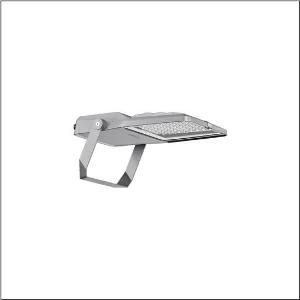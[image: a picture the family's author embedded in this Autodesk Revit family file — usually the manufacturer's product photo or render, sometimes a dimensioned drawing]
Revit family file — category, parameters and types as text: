
# Revit family: floodlight_fl_21_iq_mini___pl64_5xa7771c4e1a_d4bc
name_source: partatom
category: Lighting Fixtures
units: mm (PartAtom-declared; Revit-internal decimal feet)

## family parameters
Cut with Voids When Loaded = No
Host = Face
Light Source = No
Part Type = Normal
Room Calculation Point = No
Round Connector Dimension = Use Diameter
Shared = No

## types (1)
- --- (1 x LED, 12280 lm, 87.2 W, 4000K)
    Apparent Load = 87 VA
    CIE Flux Codes = 28 80 98 100 100
    Color Rendering = 70
    Color Temperature = 4000K
    Default Elevation = 1800 mm
    Description = Floodlight FL 21 iQ mini, floodlight, primary light control with lens, of PMMA, primary optical cover: protective disc, of toughened safety glass, transparent, light distribution: PL64, light emission: direct distribution, installation type: surface-mounted, LED, High Power LED, rated luminous flux: 12.280lm, luminous efficacy: 141lm/W, light colour: 740, colour temperature: 4000K, control: Auto-Match, Temp-Guard, Lumen-Switch, Night-Set, Smart-Wire, Light-Fading, Desk-Remote (wireless, voltage-free reading and setting of iQ features in the workshop via application-optimized NFC function/RFID function), optimised constant luminous flux control (CLO 2.0), with terminal, 6-pole, mains connection: 220..240V, AC, 50/60Hz, start of lifetime: 87W, end of service life: 92W, reduction: 40W, luminaire housing, of diecast aluminium, powder-coated, Siteco® metallic grey (DB 702S), corrosivity category C5 mid according to DIN EN ISO 12944, sealing non-destructively replaceable, mounting bracket, of steel, galvanised, powder-coated, Siteco® metallic grey (DB 702S), protection rating (complete): IP66, insulation class (complete): insulation class II (safety insulation), certification: CE, ENEC, VDE, protection symbol: D, impact resistance: IK08, permissible operating ambient temperature: -40..+40°C, permissible operating ambient temperature for outdoor applications: -40..+50°C, standard: DIN EN 12944, LABS conformity tested according to VDMA 24364:2018-05, packaging unit: 1 piece

Light Distribution: PL64
    Height = 70 mm
    Lamp = 1 x LED
    Lamp Light Flux = 12280 lm
    Lamp Power = 87.2 W
    Lamp count = 1
    Length = 485 mm
    Luminous efficacy = 141 lm/W
    Manufacturer = Siteco
    ModVariant = No
    Model = 5XA7771C4E1A
    Number of Poles = 1
    OnlyDefault = Yes
    Power Factor = 1
    Product Name = Floodlight FL 21 iQ mini | PL64
    Product group = floodlight | pylon annexe
    ProductGroupID = 6200
    Protection Class = Protection class II
    Protection Degree = IP 66
    RLX_Detail_Level = 1
    RLX_Emergency_Light_Flux = 0 lm
    RLX_Emergency_Type = 0
    RLX_Emergency_Type_DB = No
    RlxData = <blob elided: 96209 chars, md5=9c8d874e>
    Socket = socket
    Standby Power = 0 W
    System Light Flux = 12280 lm
    System Power = 87 W
    Type Comments = factory setting: luminous flux: 100 % | dim-lin: 254 | 456 mA
    Type Image = l_1006845.jpg
    URL = http://relux.com
    VarID = @adj_116729
    Voltage = 0 V
    Weight = 0.00 kg
    Width = 337 mm

## geometry (parser evidence)
native form markers: Blend x4, Sweep x12
no freeform markers — native parametric forms only
